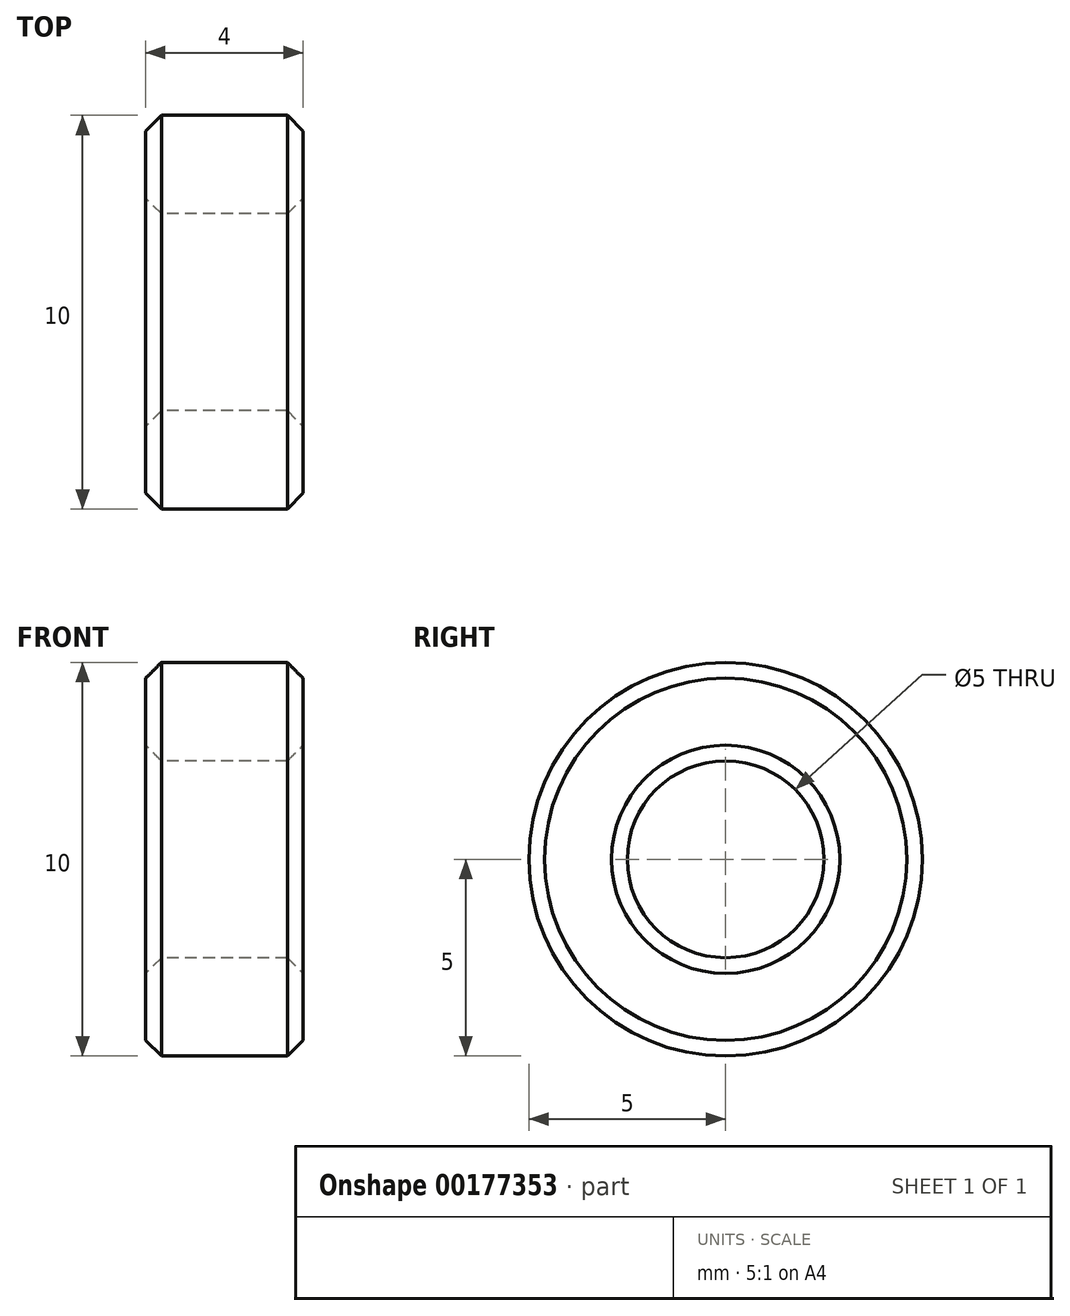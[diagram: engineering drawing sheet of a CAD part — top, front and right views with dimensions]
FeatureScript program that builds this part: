
annotation { "Feature Type Name" : "Feature", "Feature Type Description" : "" }
export const myFeature = defineFeature(function(context is Context, id is Id, definition is map)
    precondition{}
    {
        {
            var Q0;
            Q0=qCreatedBy(makeId("Front.planeOp"),FACE);
            var sketch = newSketch(context, id + "F0", { "sketchPlane" : qUnion([Q0])});
            skLineSegment(sketch, "E0.bottom", {"start": v(0, 2.5) * mm, "end": v(4, 2.5) * mm});
            skLineSegment(sketch, "E0.top", {"start": v(0, 5) * mm, "end": v(4, 5) * mm});
            skLineSegment(sketch, "E0.left", {"start": v(0, 2.5) * mm, "end": v(0, 5) * mm});
            skLineSegment(sketch, "E0.right", {"start": v(4, 2.5) * mm, "end": v(4, 5) * mm});
            skLineSegment(sketch, "E1", {"start": v(0, 0) * mm, "end": v(2.72, 0) * mm, "construction": true});
            skSolve(sketch);
        }
        {
            var Q0;
            Q0 = qSketchRegion(id + "F0", true);
            var Q1;
            Q1=sQuery(id+"F0.wireOp",EDGE,"E1");
            revolve(context, id + "F1", {"surfaceOperationType" : NewSurfaceOperationType.NEW, "entities" : qUnion([Q0]), "axis" : qUnion([Q1]), "revolveType" : RevolveType.FULL});
        }
        {
            var Q0;
            Q0=makeQuery(id+"F1.opRevolve","SWEPT_FACE",FACE,{"disambiguationData":[OSD([sQuery(id+"F0.wireOp",EDGE,"E0.bottom")])]});
            var Q1;
            Q1=makeQuery(id+"F1.opRevolve","SWEPT_FACE",FACE,{"disambiguationData":[OSD([sQuery(id+"F0.wireOp",EDGE,"E0.top")])]});
            chamfer(context, id + "F2", {"entities" : qUnion([Q0, Q1]), "width" : 0.4 * mm, "tangentPropagation" : true});
        }
    });
